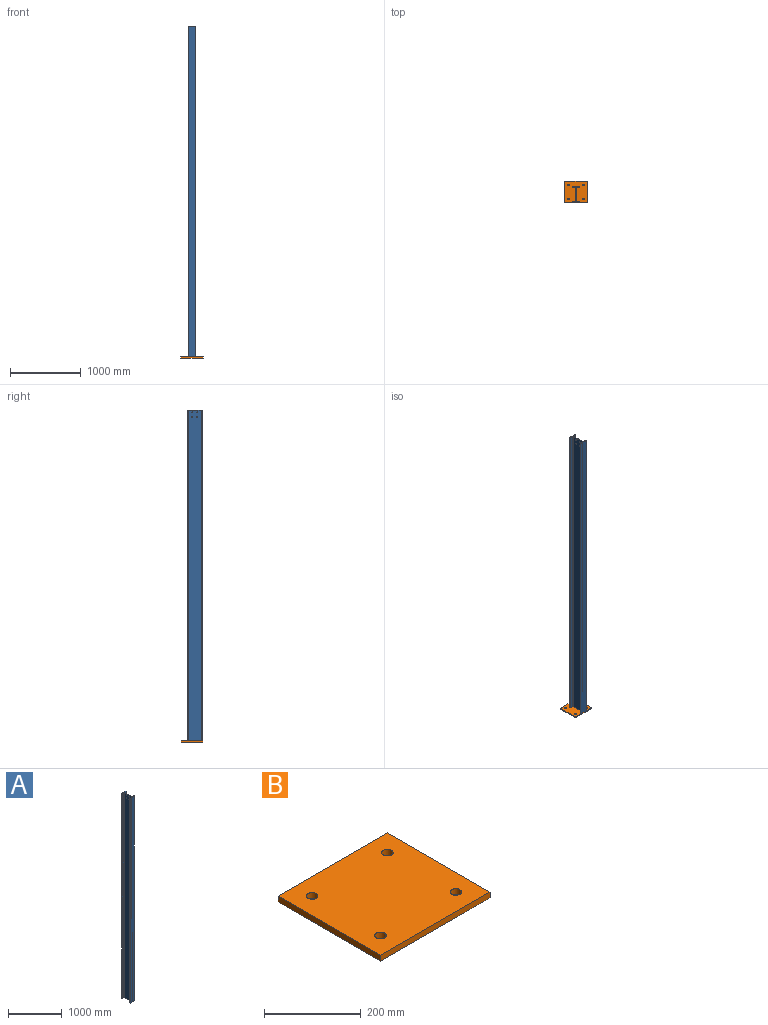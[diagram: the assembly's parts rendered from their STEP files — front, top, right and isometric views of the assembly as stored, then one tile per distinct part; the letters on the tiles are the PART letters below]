
ASSEMBLY  parts=2 mates=1
PART A: 22 faces, bbox 110x220x4685 mm
  f0: plane 220x110mm, normal (0,0,-1), area 3337.1mm2, adj f2,f3,f4,f5,f6,f7,f8,f9
  f1: plane 220x110mm, normal (0,0,1), area 3337.1mm2, adj f2,f3,f4,f5,f6,f7,f8,f9
  f2: plane 4685x40.05mm, normal (0,1,0), area 187634.2mm2, adj f0,f1,f3,f17
  f3: cylinder r=12mm len=4685mm, axis (0,0,1), area 88310.3mm2, adj f0,f1,f2,f4
  f4: plane 4685x177.6mm, normal (1,0,0), area 831440.2mm2, adj f0,f1,f3,f5,f18,f19,f20,f21
  f5: cylinder r=12mm len=4685mm, axis (0,0,1), area 88310.3mm2, adj f0,f1,f4,f6
  f6: plane 4685x40.05mm, normal (0,-1,0), area 187634.2mm2, adj f0,f1,f5,f7
  f7: plane 4685x9.2mm, normal (1,0,0), area 43102mm2, adj f0,f1,f6,f8
  f8: plane 4685x110mm, normal (0,1,0), area 515350mm2, adj f0,f1,f7,f9
  f9: plane 4685x9.2mm, normal (-1,0,0), area 43102mm2, adj f0,f1,f8,f10
  f10: plane 4685x40.05mm, normal (0,-1,0), area 187634.2mm2, adj f0,f1,f9,f11
  f11: cylinder r=12mm len=4685mm, axis (0,0,1), area 88310.3mm2, adj f0,f1,f10,f12
  f12: plane 4685x177.6mm, normal (-1,0,0), area 831440.2mm2, adj f0,f1,f11,f13,f18,f19,f20,f21
  f13: cylinder r=12mm len=4685mm, axis (0,0,1), area 88310.3mm2, adj f0,f1,f12,f14
  f14: plane 4685x40.05mm, normal (0,1,0), area 187634.2mm2, adj f0,f1,f13,f15
  f15: plane 4685x9.2mm, normal (-1,0,0), area 43102mm2, adj f0,f1,f14,f16
  f16: plane 4685x110mm, normal (0,-1,0), area 515350mm2, adj f0,f1,f15,f17
  f17: plane 4685x9.2mm, normal (1,0,0), area 43102mm2, adj f0,f1,f2,f16
  f18: cylinder r=7mm len=14mm, axis (-1,0,0), area 259.5mm2, adj f4,f12
  f19: cylinder r=7mm len=14mm, axis (-1,0,0), area 259.5mm2, adj f4,f12
  f20: cylinder r=7mm len=14mm, axis (-1,0,0), area 259.5mm2, adj f4,f12
  f21: cylinder r=7mm len=14mm, axis (-1,0,0), area 259.5mm2, adj f4,f12
PART B: 10 faces, bbox 320x300x15 mm
  f0: cylinder r=12mm len=24mm, axis (0,0,-1), area 1131mm2, adj f4,f5
  f1: cylinder r=12mm len=24mm, axis (0,0,-1), area 1131mm2, adj f4,f5
  f2: cylinder r=12mm len=24mm, axis (0,0,-1), area 1131mm2, adj f4,f5
  f3: cylinder r=12mm len=24mm, axis (0,0,-1), area 1131mm2, adj f4,f5
  f4: plane 320x300mm, normal (0,0,1), area 94190.4mm2, adj f0,f1,f2,f3,f6,f7,f8,f9
  f5: plane 320x300mm, normal (0,0,-1), area 94190.4mm2, adj f0,f1,f2,f3,f6,f7,f8,f9
  f6: plane 300x15mm, normal (-1,0,0), area 4500mm2, adj f4,f5,f7,f9
  f7: plane 320x15mm, normal (0,-1,0), area 4800mm2, adj f4,f5,f6,f8
  f8: plane 300x15mm, normal (1,0,0), area 4500mm2, adj f4,f5,f7,f9
  f9: plane 320x15mm, normal (0,1,0), area 4800mm2, adj f4,f5,f6,f8
PLACE A at identity
PLACE B t=(6134,-110,0)mm
MATE fastened B.f4 <-> A.f0  axis (0,0,1) through (6294,-110,15)mm
